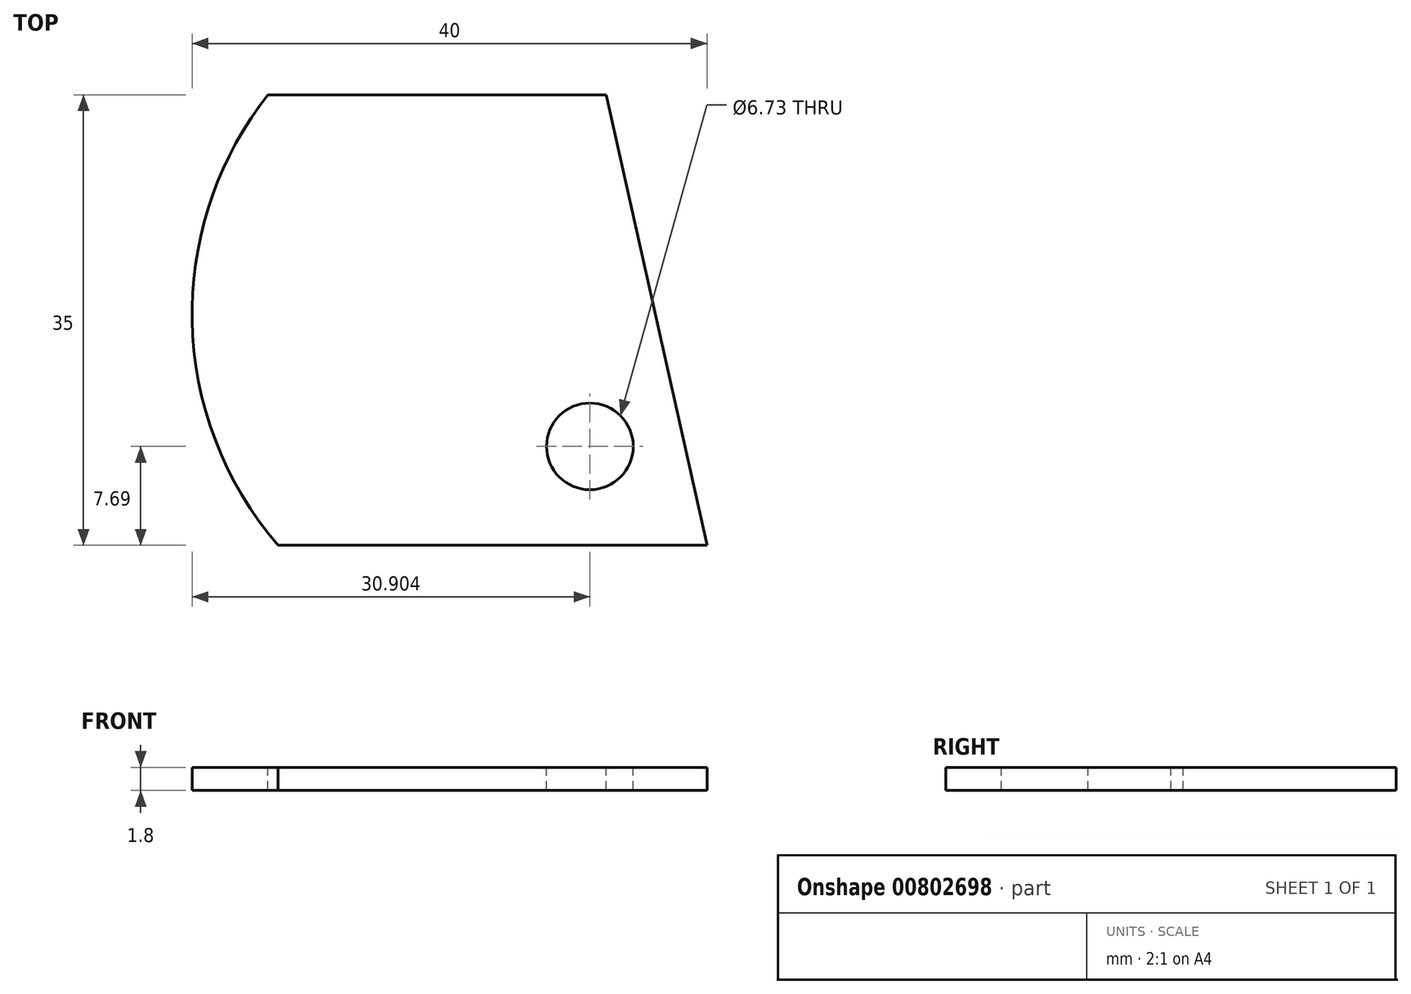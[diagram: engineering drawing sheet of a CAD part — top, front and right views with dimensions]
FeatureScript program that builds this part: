
annotation { "Feature Type Name" : "Feature", "Feature Type Description" : "" }
export const myFeature = defineFeature(function(context is Context, id is Id, definition is map)
    precondition{}
    {
        {
            var Q0;
            Q0=qCreatedBy(makeId("Top.planeOp"),FACE);
            var sketch = newSketch(context, id + "F0", { "sketchPlane" : qUnion([Q0])});
            skLineSegment(sketch, "E0.bottom", {"start": v(-20, -17.5) * mm, "end": v(20, -17.5) * mm});
            skLineSegment(sketch, "E0.top", {"start": v(-20, 17.5) * mm, "end": v(20, 17.5) * mm});
            skLineSegment(sketch, "E0.left", {"start": v(-20, -17.5) * mm, "end": v(-20, 17.5) * mm});
            skLineSegment(sketch, "E0.right", {"start": v(20, -17.5) * mm, "end": v(20, 17.5) * mm});
            skPoint(sketch, "E0.middle", {"position": v(0, 0) * mm});
            skSolve(sketch);
        }
        {
            var Q0;
            Q0 = qSketchRegion(id + "F0", true);
            extrude(context, id + "F1", {"entities" : qUnion([Q0]), "depth" : 1.8 * mm, "offsetDistance" : 25 * mm});
        }
        {
            var Q0;
            Q0=makeQuery(id+"F1.opExtrude","CAP_FACE",FACE,{"disambiguationData":[OSD([sQuery(id+"F0.wireOp",EDGE,"E0.bottom"),sQuery(id+"F0.wireOp",EDGE,"E0.top"),sQuery(id+"F0.wireOp",EDGE,"E0.left"),sQuery(id+"F0.wireOp",EDGE,"E0.right")])],"isStart":false});
            var sketch = newSketch(context, id + "F2", { "sketchPlane" : qUnion([Q0])});
            skLineSegment(sketch, "E1", {"start": v(12.17, 17.5) * mm, "end": v(20, -17.5) * mm});
            skSolve(sketch);
        }
        {
            var Q0;
            Q0 = qSketchRegion(id + "F2", true);
            var Q1;
            {var subQ0=sQuery(id+"F2.wireOp",EDGE,"E1");Q1=makeQuery(id+"F2.imprint","IMPRINT",FACE,{"disambiguationData":[TD([[makeQuery(id+"F2.imprint","IMPRINT",EDGE,{"derivedFrom":subQ0}),1.0]])]});}
            extrude(context, id + "F3", {"entities" : qUnion([Q0, Q1]), "operationType" : NewBodyOperationType.REMOVE, "endBound" : BoundingType.THROUGH_ALL, "oppositeDirection" : true, "depth" : 25 * mm, "offsetDistance" : 25 * mm});
        }
        {
            var Q0;
            Q0=makeQuery(id+"F1.opExtrude","CAP_FACE",FACE,{"disambiguationData":[OSD([sQuery(id+"F0.wireOp",EDGE,"E0.bottom"),sQuery(id+"F0.wireOp",EDGE,"E0.top"),sQuery(id+"F0.wireOp",EDGE,"E0.left"),sQuery(id+"F0.wireOp",EDGE,"E0.right")])],"isStart":false});
            var sketch = newSketch(context, id + "F4", { "sketchPlane" : qUnion([Q0])});
            skArc(sketch, "E2", {"start": v(-14.1, 17.5) * mm, "mid": v(-20, -0.14) * mm, "end": v(-13.31, -17.5) * mm});
            skSolve(sketch);
        }
        {
            var Q0;
            {var subQ0=sQuery(id+"F4.wireOp",EDGE,"E2");var subQ1=makeQuery(id+"F7uV3EvnzdVP31F_1.imprint","IMPRINT",EDGE,{"derivedFrom":makeQuery(id+"F1.opExtrude","CAP_EDGE",EDGE,{"disambiguationData":[OSD([sQuery(id+"F0.wireOp",EDGE,"E0.bottom")])],"isStart":false})});var subQ2=makeQuery(id+"F4.imprint","INTERSECT",VERTEX,{"derivedFrom":[subQ1,subQ0]});Q0=makeQuery(id+"F4.imprint","IMPRINT",FACE,{"disambiguationData":[TD([[makeQuery(id+"F4.imprint","IMPRINT",EDGE,{"disambiguationData":[TD([[subQ2,1.0]])],"derivedFrom":subQ0}),-1.0]])]});}
            var Q1;
            {var subQ0=sQuery(id+"F4.wireOp",EDGE,"E2");var subQ1=makeQuery(id+"F7uV3EvnzdVP31F_1.imprint","IMPRINT",EDGE,{"derivedFrom":makeQuery(id+"F1.opExtrude","CAP_EDGE",EDGE,{"disambiguationData":[OSD([sQuery(id+"F0.wireOp",EDGE,"E0.top")])],"isStart":false})});var subQ2=makeQuery(id+"F4.imprint","INTERSECT",VERTEX,{"derivedFrom":[subQ1,subQ0]});Q1=makeQuery(id+"F4.imprint","IMPRINT",FACE,{"disambiguationData":[TD([[makeQuery(id+"F4.imprint","IMPRINT",EDGE,{"disambiguationData":[TD([[subQ2,-1.0]])],"derivedFrom":subQ0}),-1.0]])]});}
            extrude(context, id + "F5", {"entities" : qUnion([Q0, Q1]), "operationType" : NewBodyOperationType.REMOVE, "endBound" : BoundingType.THROUGH_ALL, "oppositeDirection" : true, "depth" : 25 * mm, "offsetDistance" : 25 * mm});
        }
        {
            var Q0;
            Q0=makeQuery(id+"F1.opExtrude","CAP_FACE",FACE,{"disambiguationData":[OSD([sQuery(id+"F0.wireOp",EDGE,"E0.bottom"),sQuery(id+"F0.wireOp",EDGE,"E0.top"),sQuery(id+"F0.wireOp",EDGE,"E0.left"),sQuery(id+"F0.wireOp",EDGE,"E0.right")])],"isStart":false});
            var sketch = newSketch(context, id + "F6", { "sketchPlane" : qUnion([Q0])});
            skCircle(sketch, "E3", {"center": v(10.9, -9.8) * mm, "radius": 3.37 * mm});
            skSolve(sketch);
        }
        {
            var Q0;
            Q0=makeQuery(id+"F6.imprint","IMPRINT",FACE,{"disambiguationData":[TD([[makeQuery(id+"F6.imprint","IMPRINT",EDGE,{"derivedFrom":sQuery(id+"F6.wireOp",EDGE,"E3")}),1.0]])]});
            extrude(context, id + "F7", {"entities" : qUnion([Q0]), "operationType" : NewBodyOperationType.REMOVE, "endBound" : BoundingType.THROUGH_ALL, "oppositeDirection" : true, "depth" : 25 * mm, "offsetDistance" : 25 * mm});
        }
    });
